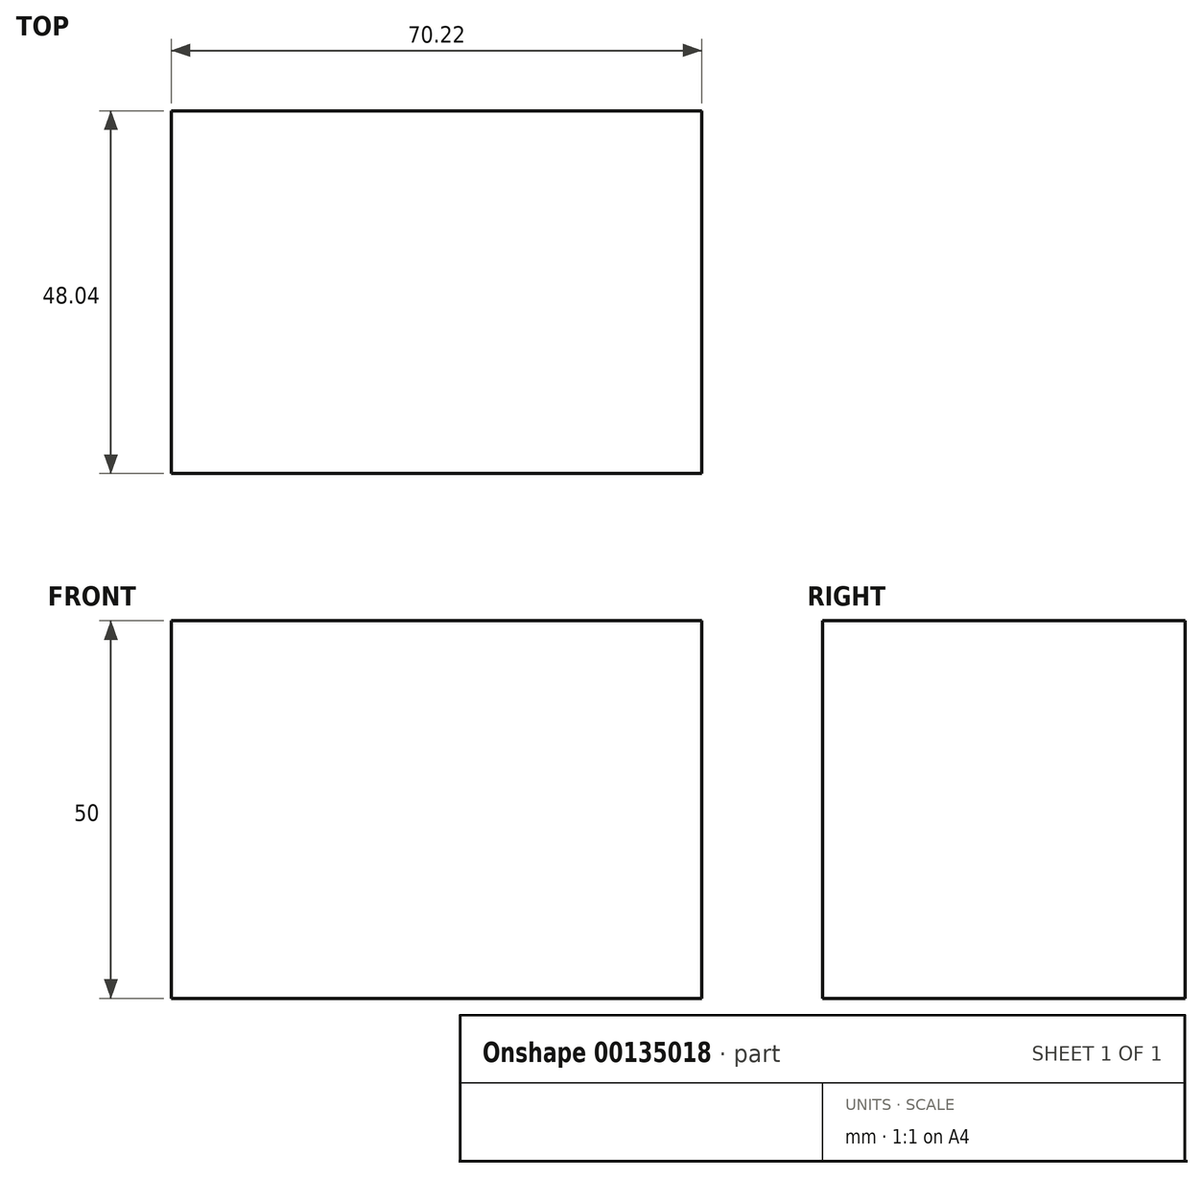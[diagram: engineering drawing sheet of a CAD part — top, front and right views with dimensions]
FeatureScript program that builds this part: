
annotation { "Feature Type Name" : "Feature", "Feature Type Description" : "" }
export const myFeature = defineFeature(function(context is Context, id is Id, definition is map)
    precondition{}
    {
        {
            var Q0;
            Q0=qCreatedBy(makeId("Top.planeOp"),FACE);
            var sketch = newSketch(context, id + "F0", { "sketchPlane" : qUnion([Q0])});
            skLineSegment(sketch, "E0.bottom", {"start": v(-26.98, 17.35) * mm, "end": v(43.24, 17.35) * mm});
            skLineSegment(sketch, "E0.top", {"start": v(-26.98, -30.69) * mm, "end": v(43.24, -30.69) * mm});
            skLineSegment(sketch, "E0.left", {"start": v(-26.98, 17.35) * mm, "end": v(-26.98, -30.69) * mm});
            skLineSegment(sketch, "E0.right", {"start": v(43.24, 17.35) * mm, "end": v(43.24, -30.69) * mm});
            skSolve(sketch);
        }
        {
            var Q0;
            Q0 = qSketchRegion(id + "F0", true);
            extrude(context, id + "F1", {"entities" : qUnion([Q0]), "depth" : 50 * mm});
        }
    });
